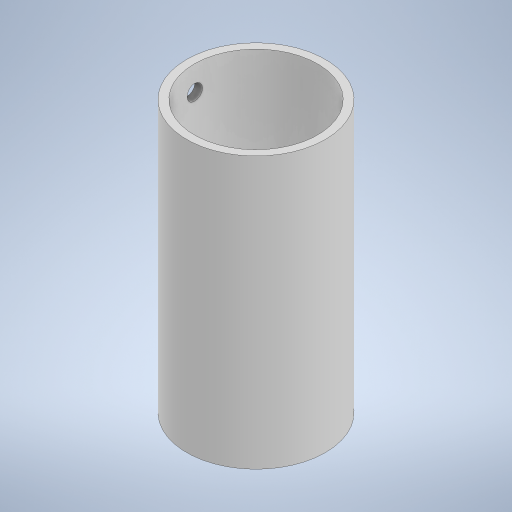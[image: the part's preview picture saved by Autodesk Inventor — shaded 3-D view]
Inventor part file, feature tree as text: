
AUTODESK INVENTOR PART (.ipt)
format: ipt  version: 2023 (Build 270158000, 158)  size: 221,696 bytes
history: native  units: in
note: dims shown in document units (in); Inventor stores cm internally (conversion verified against a paired STEP export)
features: extrude x2, sketch x2
ambient origin geometry x8: Origin, YZ Plane, XZ Plane, XY Plane, X Axis, Y Axis, Z Axis, Center Point
bodies: Solid1 (feature_tree)
feature tree (4):
  extrude  "Extrusion1"  Depth=0.25in
  extrude  "Extrusion2"  Depth=0.55in
  sketch  "Sketch1"  dims[d0=0.2812in d1=0.25in]
  sketch  "Sketch2"  dims[d2=0.55in d3=0.0in d4=0.0312in d5=1.0in d6=0.0in d8=0.05in]
